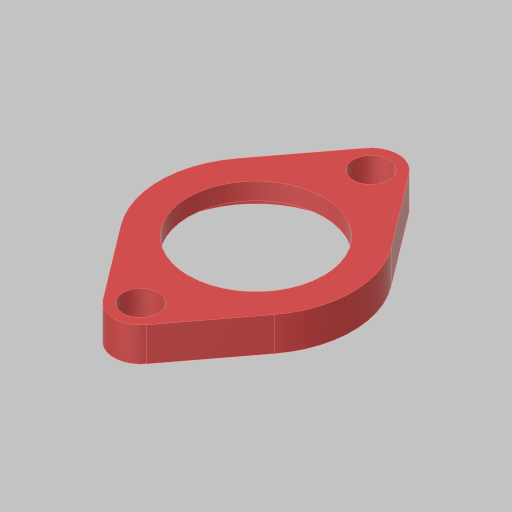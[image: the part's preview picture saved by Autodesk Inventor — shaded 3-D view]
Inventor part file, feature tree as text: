
AUTODESK INVENTOR PART (.ipt)
format: ipt  version: 2023.5 (Build 275446000, 446)  size: 125,952 bytes
history: native  units: in
note: dims shown in document units (in); Inventor stores cm internally (conversion verified against a paired STEP export)
features: extrude x2, sketch x1, hole x1
ambient origin geometry x8: Origin, YZ Plane, XZ Plane, XY Plane, X Axis, Y Axis, Z Axis, Center Point
bodies: Solid1 (feature_tree)
feature tree (4):
  sketch  "Sketch1"  dims[d0=1.0in d1=1.425in d2=0.4in d3=0.25in d4=0.0in d5=0.125in d6=0.0in d7=1.3in d8=0.2638in d9=0.38in d10=0.385in d11=0.25in d12=0.5635in d13=1.0in d14=0.8108in d15=1.7in]
  extrude  "Extrusion1"  Depth=1.425in
  extrude  "Extrusion2"  Depth=0.25in
  hole  "Hole1"  [1 undecoded]
note: 1 required parameter value undecoded (feature->parameter linkage not recoverable at this tier; creation-order binding heuristic only, values carry confidence <= 0.55)
